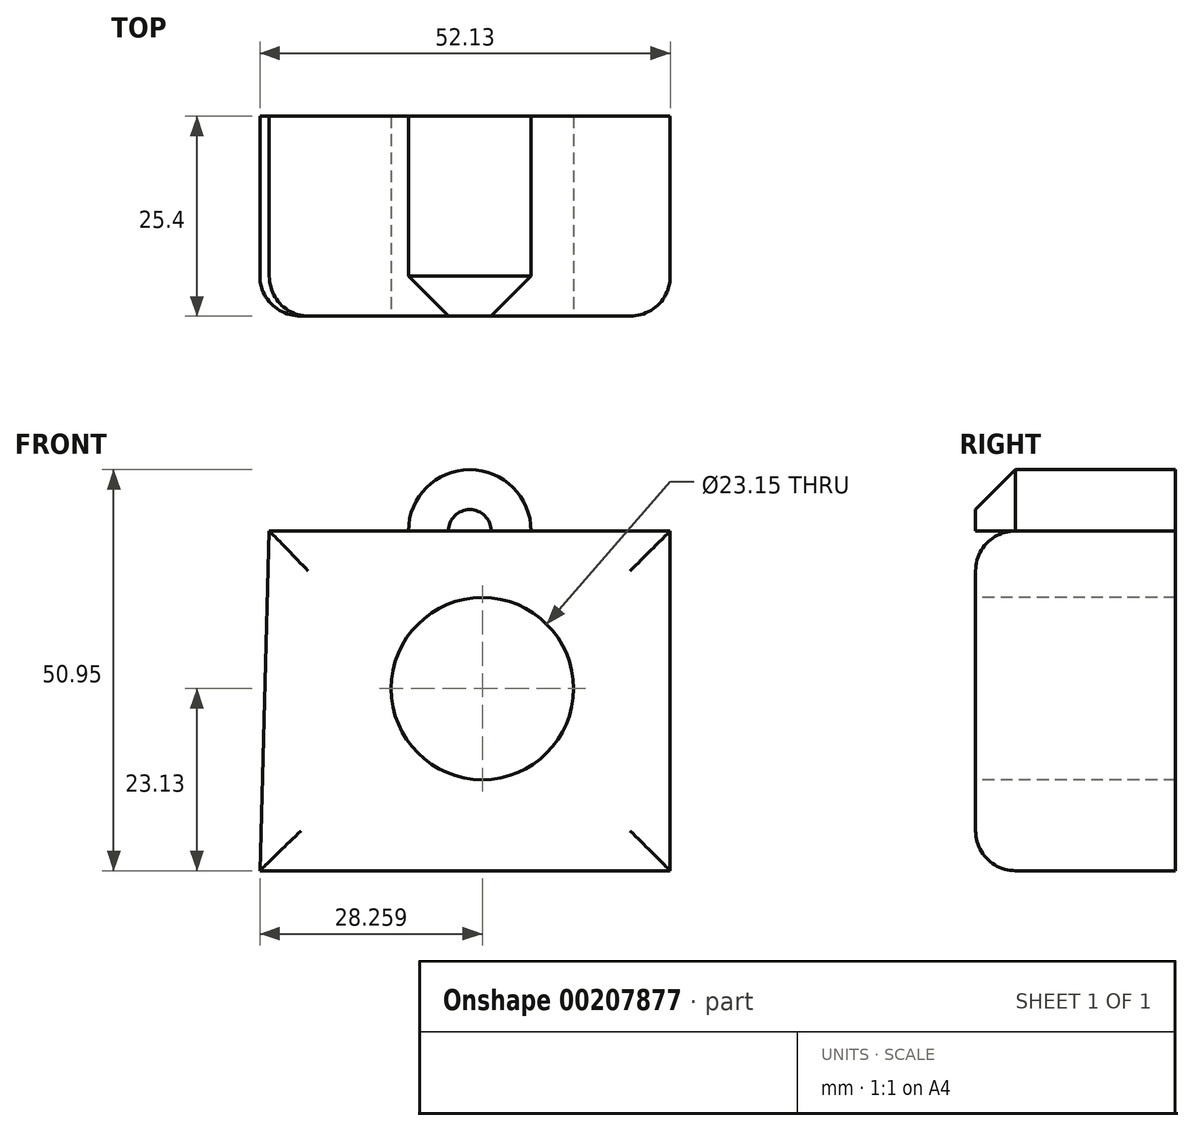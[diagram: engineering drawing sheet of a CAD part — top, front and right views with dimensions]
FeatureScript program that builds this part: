
annotation { "Feature Type Name" : "Feature", "Feature Type Description" : "" }
export const myFeature = defineFeature(function(context is Context, id is Id, definition is map)
    precondition{}
    {
        {
            var Q0;
            Q0=qCreatedBy(makeId("Front.planeOp"),FACE);
            var sketch = newSketch(context, id + "F0", { "sketchPlane" : qUnion([Q0])});
            skLineSegment(sketch, "E0", {"start": v(-65.4, 56.18) * mm, "end": v(-14.48, 56.18) * mm});
            skLineSegment(sketch, "E1", {"start": v(-14.48, 56.18) * mm, "end": v(-14.48, 13) * mm});
            skLineSegment(sketch, "E2", {"start": v(-14.48, 13) * mm, "end": v(-66.61, 13) * mm});
            skLineSegment(sketch, "E3", {"start": v(-66.61, 13) * mm, "end": v(-65.4, 56.18) * mm});
            skSolve(sketch);
        }
        {
            var Q0;
            Q0=makeQuery(id+"F0.imprint","IMPRINT",FACE,{"disambiguationData":[TD([[makeQuery(id+"F0.imprint","IMPRINT",EDGE,{"derivedFrom":sQuery(id+"F0.wireOp",EDGE,"E0")}),-1.0]])]});
            extrude(context, id + "F1", {"entities" : qUnion([Q0]), "depth" : 25.4 * mm});
        }
        {
            var Q0;
            Q0=makeQuery(id+"F1.opExtrude","CAP_FACE",FACE,{"disambiguationData":[OSD([sQuery(id+"F0.wireOp",EDGE,"E0"),sQuery(id+"F0.wireOp",EDGE,"E1"),sQuery(id+"F0.wireOp",EDGE,"E2"),sQuery(id+"F0.wireOp",EDGE,"E3")])],"isStart":false});
            var sketch = newSketch(context, id + "F2", { "sketchPlane" : qUnion([Q0])});
            skCircle(sketch, "E4", {"center": v(-39.94, 56.18) * mm, "radius": 7.78 * mm});
            skSolve(sketch);
        }
        {
            var Q0;
            {var subQ0=sQuery(id+"F2.wireOp",EDGE,"E4");var subQ1=makeQuery(id+"F1.opExtrude","CAP_EDGE",EDGE,{"disambiguationData":[OSD([sQuery(id+"F0.wireOp",EDGE,"E0")])],"isStart":false});var subQ2=makeQuery(id+"F2.imprint","INTERSECT",VERTEX,{"disambiguationData":[OD(0.0)],"derivedFrom":[subQ1,subQ0]});Q0=makeQuery(id+"F2.imprint","IMPRINT",FACE,{"disambiguationData":[TD([[makeQuery(id+"F2.imprint","IMPRINT",EDGE,{"disambiguationData":[TD([[subQ2,1.0]])],"derivedFrom":subQ0}),1.0]])]});}
            var Q1;
            Q1=sQuery(id+"F2.wireOp",EDGE,"E4");
            extrude(context, id + "F3", {"entities" : qUnion([Q0]), "surfaceEntities" : qUnion([Q1]), "oppositeDirection" : true, "depth" : 25.4 * mm});
        }
        {
            var Q0;
            Q0=makeQuery(id+"F1.opExtrude","CAP_FACE",FACE,{"disambiguationData":[OSD([sQuery(id+"F0.wireOp",EDGE,"E0"),sQuery(id+"F0.wireOp",EDGE,"E1"),sQuery(id+"F0.wireOp",EDGE,"E2"),sQuery(id+"F0.wireOp",EDGE,"E3")])],"isStart":false});
            var sketch = newSketch(context, id + "F4", { "sketchPlane" : qUnion([Q0])});
            skCircle(sketch, "E5", {"center": v(-38.35, 36.14) * mm, "radius": 11.57 * mm});
            skSolve(sketch);
        }
        {
            var Q0;
            Q0 = qSketchRegion(id + "F4", true);
            extrude(context, id + "F5", {"entities" : qUnion([Q0]), "operationType" : NewBodyOperationType.ADD, "endBound" : BoundingType.THROUGH_ALL, "depth" : 25.4 * mm});
        }
        {
            var Q0;
            Q0=makeQuery(id+"F5.opExtrude","CAP_FACE",FACE,{"disambiguationData":[OSD([sQuery(id+"F4.wireOp",EDGE,"E5")])],"isStart":false});
            extrude(context, id + "F6", {"entities" : qUnion([Q0]), "operationType" : NewBodyOperationType.REMOVE, "endBound" : BoundingType.THROUGH_ALL, "oppositeDirection" : true, "depth" : 25.4 * mm});
        }
        {
            var Q0;
            Q0=makeQuery(id+"F1.opExtrude","CAP_EDGE",EDGE,{"disambiguationData":[OSD([sQuery(id+"F0.wireOp",EDGE,"E1")])],"isStart":false});
            var Q1;
            Q1=makeQuery(id+"F1.opExtrude","CAP_EDGE",EDGE,{"disambiguationData":[OSD([sQuery(id+"F0.wireOp",EDGE,"E2")])],"isStart":false});
            var Q2;
            Q2=makeQuery(id+"F1.opExtrude","CAP_EDGE",EDGE,{"disambiguationData":[OSD([sQuery(id+"F0.wireOp",EDGE,"E3")])],"isStart":false});
            var Q3;
            Q3=makeQuery(id+"F1.opExtrude","CAP_EDGE",EDGE,{"disambiguationData":[OSD([sQuery(id+"F0.wireOp",EDGE,"E0")])],"isStart":false});
            fillet(context, id + "F7", {"entities" : qUnion([Q0, Q1, Q2, Q3]), "radius" : 5.08 * mm, "tangentPropagation" : true, "allowEdgeOverflow" : false});
        }
        {
            var Q0;
            Q0=makeQuery(id+"F3.opExtrude","CAP_EDGE",EDGE,{"disambiguationData":[OSD([sQuery(id+"F2.wireOp",EDGE,"E4")])],"isStart":true});
            chamfer(context, id + "F8", {"entities" : qUnion([Q0]), "width" : 5.08 * mm, "tangentPropagation" : true});
        }
    });
